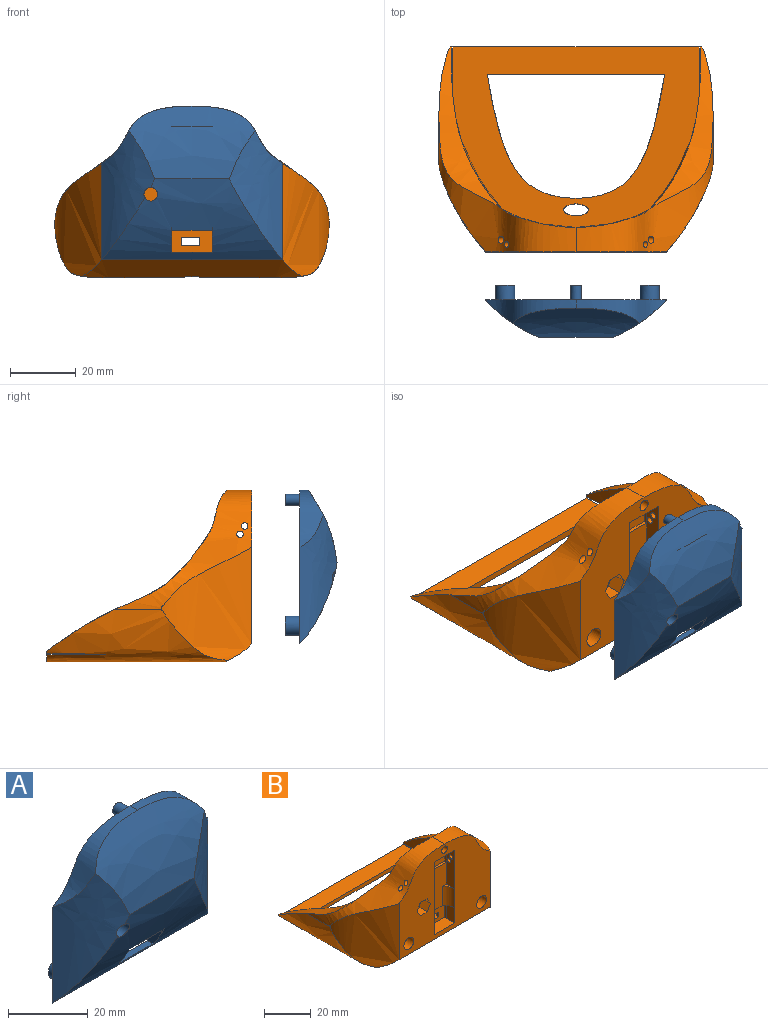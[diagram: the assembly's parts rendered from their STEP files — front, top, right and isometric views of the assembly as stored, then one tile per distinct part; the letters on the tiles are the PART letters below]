
ASSEMBLY  parts=2 mates=1
PART A: 31 faces, bbox 59.5x15.9x46.9 mm
  f0: extruded ~39.25x16.09mm, area 443.4mm2, adj f1,f2,f13,f20,f30
  f1: extruded ~54.99x24.7mm, area 942mm2, adj f0,f2,f10,f11,f12,f13,f18,f21
  f2: plane 59.44x46.82mm, normal (0,1,0), area 1742.2mm2, adj f0,f1,f17,f18,f19,f20,f21,f22
  f3: plane 12.3x1.1mm, normal (0,0,1), area 13.5mm2, adj f6,f14,f15,f16
  f4: cylinder r=6.15mm len=10mm, axis (0,0,1), area 58.1mm2, adj f5,f6,f9,f23
  f5: plane 4.98x2.55mm, normal (0,0,1), area 3.8mm2, adj f4,f6,f23
  f6: plane 21.5x12.3mm, normal (0,1,0), area 213.4mm2, adj f3,f4,f5,f7,f8,f9,f22,f23
  f7: plane 4.96x2.55mm, normal (0,0,1), area 3.8mm2, adj f6,f8,f22
  f8: cylinder r=6.15mm len=10mm, axis (0,0,1), area 57.9mm2, adj f6,f7,f9,f22
  f9: plane 12.3x6.08mm, normal (0,0,-1), area 21.2mm2, adj f4,f6,f8,f10,f11,f12,f22,f23
  f10: plane 3.34x1.11mm, normal (-1,0,0), area 2.6mm2, adj f1,f9,f11,f22
  f11: plane 12.3x1.27mm, normal (0,1,0), area 15.7mm2, adj f1,f9,f10,f12
  f12: plane 3.34x1.11mm, normal (1,0,0), area 2.6mm2, adj f1,f9,f11,f23
  f13: extruded ~38.56x22.13mm, area 714.3mm2, adj f0,f1,f18,f19,f20
  f14: plane 8.7x1.1mm, normal (1,0,0), area 9.6mm2, adj f3,f15,f17,f23
  f15: plane 12.3x8.7mm, normal (0,1,0), area 107mm2, adj f3,f14,f16,f17
  f16: plane 8.7x1.1mm, normal (-1,0,0), area 9.6mm2, adj f3,f15,f17,f22
  f17: plane 12.3x6.1mm, normal (0,0,-1), area 75mm2, adj f2,f14,f15,f16,f22,f23
  f18: extruded ~39.25x16.09mm, area 446.4mm2, adj f1,f2,f13,f19
  f19: extruded ~27.5x17.45mm, area 139.3mm2, adj f2,f13,f18,f20
  f20: extruded ~27.5x17.45mm, area 139.2mm2, adj f0,f2,f13,f19
  f21: plane 12.3x2.03mm, normal (0,0,1), area 25mm2, adj f1,f2,f22,f23
  f22: plane 38.2x5.1mm, normal (-1,0,0), area 134.5mm2, adj f1,f2,f6,f7,f8,f9,f10,f16
  f23: plane 38.12x5.02mm, normal (1,0,0), area 134.3mm2, adj f1,f2,f4,f5,f6,f9,f12,f14
  f24: cylinder r=2.9mm len=5.8mm, axis (0,-1,0), area 82mm2, adj f2,f25
  f25: plane 5.8x5.8mm, normal (0,1,0), area 26.4mm2, adj f24
  f26: cylinder r=2.9mm len=5.8mm, axis (0,-1,0), area 82mm2, adj f2,f27
  f27: plane 5.8x5.8mm, normal (0,1,0), area 26.4mm2, adj f26
  f28: cylinder r=1.65mm len=4.5mm, axis (0,-1,0), area 46.7mm2, adj f2,f29
  f29: plane 3.3x3.3mm, normal (0,1,0), area 8.6mm2, adj f28
  f30: cylinder r=2.08mm len=10.79mm, axis (0,1,0), area 132.1mm2, adj f0,f1,f2
PART B: 60 faces, bbox 83.9x62.9x53.4 mm
  f0: extruded ~55x50.13mm, area 2005.3mm2, adj f1,f4,f5,f6,f13,f19,f40,f41
  f1: extruded ~55x50.13mm, area 2007.1mm2, adj f0,f5,f7,f8,f12,f18,f39,f40
  f2: plane 12.3x7.9mm, normal (0,-1,0), area 83.4mm2, adj f28,f32,f36,f38,f39,f40,f41,f42
  f3: extruded ~66.41x8.15mm, area 583.2mm2, adj f4,f8,f9,f10,f24
  f4: extruded ~55.14x41.73mm, area 1704.9mm2, adj f0,f3,f5,f6,f8,f10,f11,f13
  f5: plane 76.13x55.04mm, normal (0,0,1), area 1894.8mm2, adj f0,f1,f4,f8,f11,f20,f21,f22
  f6: extruded ~41.78x41.73mm, area 604.5mm2, adj f0,f4,f7,f10,f16,f19,f24,f56
  f7: extruded ~41.78x41.73mm, area 604.5mm2, adj f1,f6,f8,f9,f15,f18,f24,f58
  f8: extruded ~55.14x41.73mm, area 1704.9mm2, adj f1,f3,f4,f5,f7,f9,f11,f12
  f9: extruded ~34.42x27.42mm, area 728.1mm2, adj f3,f7,f8,f14,f15,f24
  f10: extruded ~34.42x27.42mm, area 728.1mm2, adj f3,f4,f6,f16,f17,f24
  f11: plane 76.6x3.61mm, normal (0,1,0), area 146.8mm2, adj f4,f5,f8
  f12: plane 0.77x0.59mm, normal (0,1,0), area 0.2mm2, adj f1,f8,f18
  f13: plane 0.77x0.59mm, normal (0,1,0), area 0.2mm2, adj f0,f4,f19
  f14: plane 0.22x0.03mm, normal (1,-0.02,0), area 0mm2, adj f8,f9
  f15: plane 1.38x0.7mm, normal (1,-0.02,0), area 0.1mm2, adj f7,f9
  f16: plane 1.38x0.7mm, normal (-1,-0.02,0), area 0.1mm2, adj f6,f10
  f17: plane 0.22x0.03mm, normal (-1,-0.02,0), area 0mm2, adj f4,f10
  f18: extruded ~49.22x35.77mm, area 296.9mm2, adj f1,f7,f8,f12
  f19: extruded ~49.22x35.77mm, area 296.9mm2, adj f0,f4,f6,f13
  f20: extruded ~37.86x26.99mm, area 110.1mm2, adj f4,f5,f21,f22
  f21: plane 54.67x2.55mm, normal (0,-1,0), area 112mm2, adj f4,f5,f8,f20,f22
  f22: extruded ~37.86x26.99mm, area 110.1mm2, adj f5,f8,f20,f21
  f23: extruded ~7.45x3.62mm, area 33.7mm2, adj f4,f5,f8
  f24: plane 59.44x46.82mm, normal (0,-1,0), area 1708.5mm2, adj f3,f6,f7,f9,f10,f35,f36,f37
  f25: plane 12.3x1.1mm, normal (0,0,1), area 13.5mm2, adj f31,f33,f34,f38
  f26: plane 5x2.55mm, normal (0,0,1), area 3.8mm2, adj f27,f31,f38
  f27: cylinder r=6.17mm len=10mm, axis (0,0,1), area 58.3mm2, adj f26,f28,f31,f38
  f28: plane 12.3x6.1mm, normal (0,0,-1), area 21.2mm2, adj f2,f27,f29,f31,f32,f37,f38
  f29: cylinder r=6.17mm len=10mm, axis (0,0,1), area 58mm2, adj f28,f30,f31,f37
  f30: plane 4.97x2.55mm, normal (0,0,1), area 3.8mm2, adj f29,f31,f37
  f31: plane 21.5x12.3mm, normal (0,-1,0), area 213.4mm2, adj f25,f26,f27,f28,f29,f30,f37,f38
  f32: plane 7.9x1.1mm, normal (-1,0,0), area 8.7mm2, adj f2,f28,f36,f37
  f33: plane 8.7x1.1mm, normal (-1,0,0), area 9.6mm2, adj f25,f34,f35,f37
  f34: plane 12.3x8.7mm, normal (0,-1,0), area 107mm2, adj f25,f33,f35,f38
  f35: plane 12.3x6.1mm, normal (0,0,-1), area 75mm2, adj f24,f33,f34,f37,f38
  f36: plane 12.3x6.1mm, normal (0,0,1), area 75mm2, adj f2,f24,f32,f37,f38
  f37: plane 38.1x5mm, normal (-1,0,0), area 134.5mm2, adj f24,f28,f29,f30,f31,f32,f33,f35
  f38: plane 38.1x6.1mm, normal (1,0,0), area 152.5mm2, adj f2,f24,f25,f26,f27,f28,f31,f34
  f39: plane 2.5x1.37mm, normal (-1,0,0), area 3.4mm2, adj f1,f2,f40,f42
  f40: plane 5.51x1.41mm, normal (0,0,-1), area 7.4mm2, adj f0,f1,f2,f39,f41
  f41: plane 2.5x1.41mm, normal (1,0,0), area 3.5mm2, adj f0,f2,f40,f42
  f42: plane 5.51x1.41mm, normal (0,0,1), area 7.4mm2, adj f0,f1,f2,f39,f41
  f43: plane 5x4.04mm, normal (-0.02,0,1), area 20.2mm2, adj f24,f44,f48,f49
  f44: plane 5x3.53mm, normal (-0.87,0,0.49), area 20.2mm2, adj f24,f43,f45,f49
  f45: plane 5x3.47mm, normal (-0.86,0,-0.51), area 20.2mm2, adj f24,f44,f46,f49
  f46: plane 5x4.04mm, normal (0.02,0,-1), area 20.2mm2, adj f24,f45,f47,f49
  f47: plane 5x3.53mm, normal (0.87,0,-0.49), area 20.2mm2, adj f24,f46,f48,f49
  f48: plane 5x3.47mm, normal (0.86,0,0.51), area 20.2mm2, adj f24,f43,f47,f49
  f49: plane 8.08x7.06mm, normal (0,-1,0), area 42.4mm2, adj f43,f44,f45,f46,f47,f48
  f50: cylinder r=1.75mm len=5mm, axis (0,-1,0), area 55mm2, adj f24,f51
  f51: plane 3.5x3.5mm, normal (0,-1,0), area 9.6mm2, adj f50
  f52: cylinder r=3mm len=6mm, axis (0,-1,0), area 94.2mm2, adj f24,f53
  f53: plane 6x6mm, normal (0,-1,0), area 28.3mm2, adj f52
  f54: cylinder r=3mm len=6mm, axis (0,-1,0), area 94.2mm2, adj f24,f55
  f55: plane 6x6mm, normal (0,-1,0), area 28.3mm2, adj f54
  f56: cylinder r=1mm len=17.58mm, axis (-1,0,0), area 104.9mm2, adj f6,f38
  f57: cylinder r=1mm len=14.95mm, axis (-1,0,0), area 93.9mm2, adj f6,f38
  f58: cylinder r=1mm len=17.58mm, axis (-1,0,0), area 104.9mm2, adj f7,f37
  f59: cylinder r=1mm len=14.95mm, axis (-1,0,0), area 93.9mm2, adj f7,f37
PLACE A t=(-32.08,-50.03,-6.51)mm
PLACE B t=(-32.08,-35.42,-6.51)mm fixed
MATE slider B.f50 <-> A.f28  axis (0,-1,0) through (-32.08,-57.84,17.04)mm
